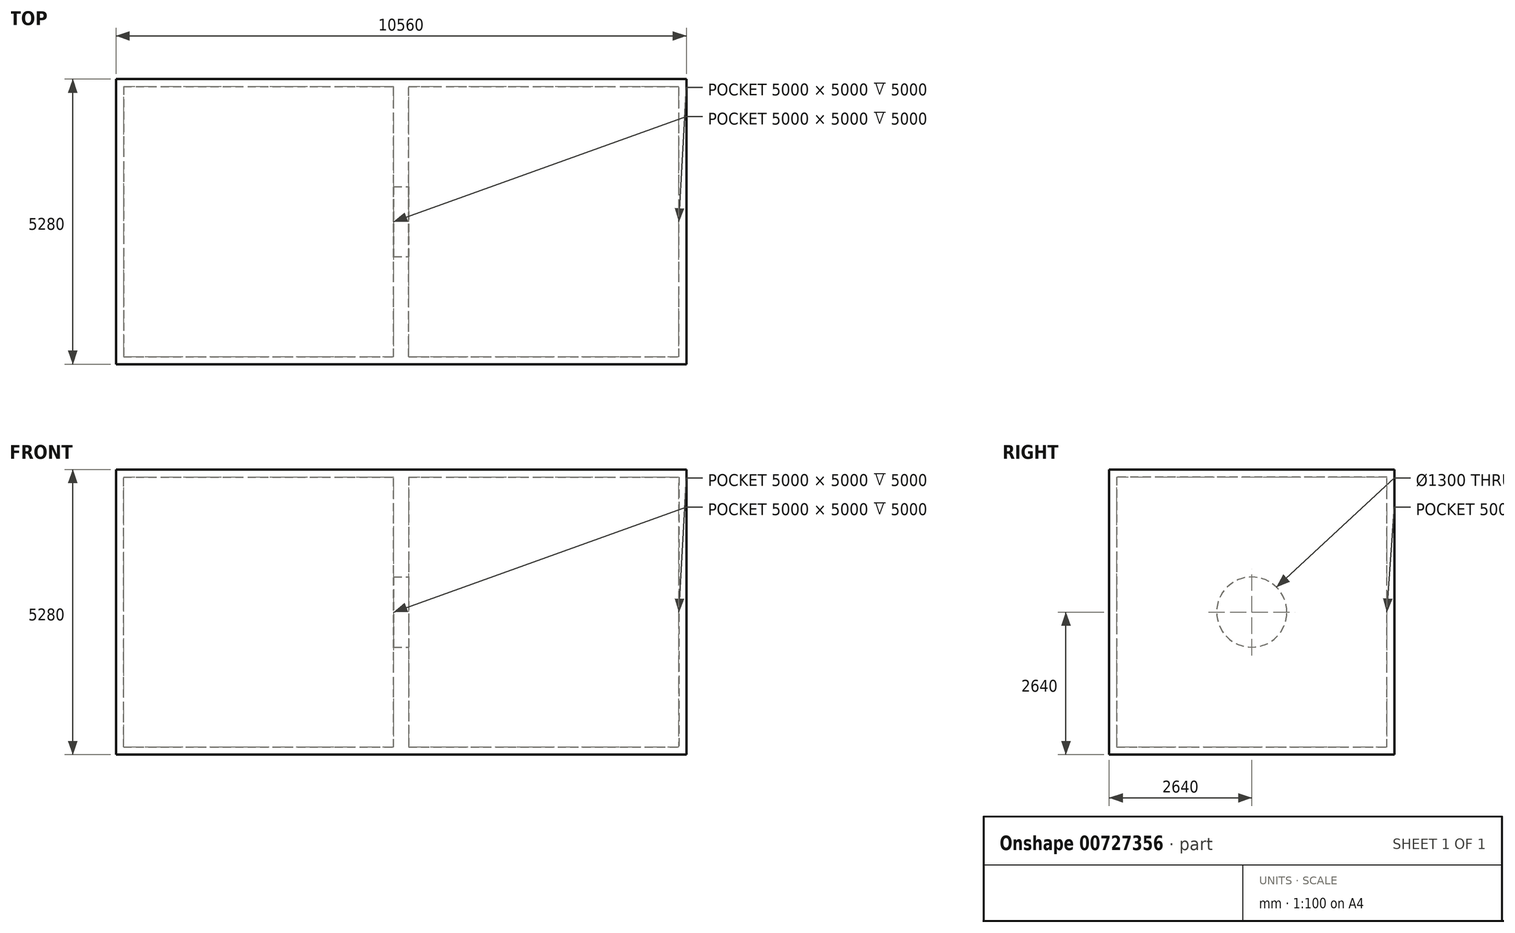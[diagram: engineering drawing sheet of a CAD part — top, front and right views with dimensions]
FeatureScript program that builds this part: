
annotation { "Feature Type Name" : "Feature", "Feature Type Description" : "" }
export const myFeature = defineFeature(function(context is Context, id is Id, definition is map)
    precondition{}
    {
        {
            var Q0;
            Q0=qCreatedBy(makeId("Right.planeOp"),FACE);
            cPlane(context, id + "F0", {"entities" : qUnion([Q0]), "cplaneType" : CPlaneType.OFFSET, "offset" : 5280 * mm, "width" : 150 * mm, "height" : 150 * mm});
        }
        {
            var Q0;
            Q0=qCreatedBy(id+"F0.planeOp",FACE);
            var sketch = newSketch(context, id + "F1", { "sketchPlane" : qUnion([Q0])});
            skLineSegment(sketch, "E0.bottom", {"start": v(-2640, 2640) * mm, "end": v(2640, 2640) * mm});
            skLineSegment(sketch, "E0.top", {"start": v(-2640, -2640) * mm, "end": v(2640, -2640) * mm});
            skLineSegment(sketch, "E0.left", {"start": v(-2640, 2640) * mm, "end": v(-2640, -2640) * mm});
            skLineSegment(sketch, "E0.right", {"start": v(2640, 2640) * mm, "end": v(2640, -2640) * mm});
            skPoint(sketch, "E0.middle", {"position": v(0, 0) * mm});
            skSolve(sketch);
        }
        {
            var Q0;
            Q0=makeQuery(id+"F1.imprint","IMPRINT",FACE,{"disambiguationData":[TD([[makeQuery(id+"F1.imprint","IMPRINT",EDGE,{"derivedFrom":sQuery(id+"F1.wireOp",EDGE,"E0.bottom")}),-1.0]])]});
            extrude(context, id + "F2", {"entities" : qUnion([Q0]), "oppositeDirection" : true, "depth" : 140 * mm, "offsetDistance" : 25 * mm});
        }
        {
            var Q0;
            Q0=makeQuery(id+"F2.opExtrude","CAP_FACE",FACE,{"disambiguationData":[OSD([sQuery(id+"F1.wireOp",EDGE,"E0.bottom"),sQuery(id+"F1.wireOp",EDGE,"E0.top"),sQuery(id+"F1.wireOp",EDGE,"E0.left"),sQuery(id+"F1.wireOp",EDGE,"E0.right")])],"isStart":false});
            var sketch = newSketch(context, id + "F3", { "sketchPlane" : qUnion([Q0])});
            skPoint(sketch, "E1", {"position": v(-2640, 2640) * mm});
            skPoint(sketch, "E2", {"position": v(2640, 2640) * mm});
            skPoint(sketch, "E3", {"position": v(2640, -2640) * mm});
            skPoint(sketch, "E4", {"position": v(-2640, -2640) * mm});
            skPoint(sketch, "E5", {"position": v(-2500, 2640) * mm});
            skPoint(sketch, "E6", {"position": v(-2640, 2500) * mm});
            skPoint(sketch, "E7", {"position": v(2500, 2640) * mm});
            skPoint(sketch, "E8", {"position": v(2640, 2500) * mm});
            skPoint(sketch, "E9", {"position": v(2640, -2500) * mm});
            skPoint(sketch, "E10", {"position": v(2500, -2640) * mm});
            skPoint(sketch, "E11", {"position": v(-2500, -2640) * mm});
            skPoint(sketch, "E12", {"position": v(-2640, -2500) * mm});
            skPoint(sketch, "E13", {"position": v(-2500, 2500) * mm});
            skPoint(sketch, "E14", {"position": v(2500, 2500) * mm});
            skPoint(sketch, "E15", {"position": v(2500, -2500) * mm});
            skPoint(sketch, "E16", {"position": v(-2500, -2500) * mm});
            skLineSegment(sketch, "E17", {"start": v(-2640, 2640) * mm, "end": v(-2640, -2640) * mm});
            skLineSegment(sketch, "E18", {"start": v(-2640, -2640) * mm, "end": v(2640, -2640) * mm});
            skLineSegment(sketch, "E19", {"start": v(2640, -2640) * mm, "end": v(2640, 2640) * mm});
            skLineSegment(sketch, "E20", {"start": v(2640, 2640) * mm, "end": v(-2640, 2640) * mm});
            skLineSegment(sketch, "E21", {"start": v(-2500, 2500) * mm, "end": v(-2500, -2500) * mm});
            skLineSegment(sketch, "E22", {"start": v(-2500, -2500) * mm, "end": v(2500, -2500) * mm});
            skLineSegment(sketch, "E23", {"start": v(2500, -2500) * mm, "end": v(2500, 2500) * mm});
            skLineSegment(sketch, "E24", {"start": v(2500, 2500) * mm, "end": v(-2500, 2500) * mm});
            skSolve(sketch);
        }
        {
            var Q0;
            Q0=makeQuery(id+"F3.imprint","IMPRINT",FACE,{"disambiguationData":[TD([[makeQuery(id+"F3.imprint","IMPRINT",EDGE,{"derivedFrom":sQuery(id+"F3.wireOp",EDGE,"E17")}),1.0]])]});
            extrude(context, id + "F4", {"entities" : qUnion([Q0]), "operationType" : NewBodyOperationType.ADD, "depth" : 5000 * mm, "offsetDistance" : 25 * mm});
        }
        {
            var Q0;
            Q0=makeQuery(id+"F4.opExtrude","CAP_FACE",FACE,{"disambiguationData":[OSD([sQuery(id+"F3.wireOp",EDGE,"E17"),sQuery(id+"F3.wireOp",EDGE,"E18"),sQuery(id+"F3.wireOp",EDGE,"E19"),sQuery(id+"F3.wireOp",EDGE,"E20"),sQuery(id+"F3.wireOp",EDGE,"E21"),sQuery(id+"F3.wireOp",EDGE,"E22"),sQuery(id+"F3.wireOp",EDGE,"E23"),sQuery(id+"F3.wireOp",EDGE,"E24")])],"isStart":false});
            var sketch = newSketch(context, id + "F5", { "sketchPlane" : qUnion([Q0])});
            skPoint(sketch, "E25", {"position": v(-2640, 2640) * mm});
            skPoint(sketch, "E26", {"position": v(2640, 2640) * mm});
            skPoint(sketch, "E27", {"position": v(2640, -2640) * mm});
            skPoint(sketch, "E28", {"position": v(-2640, -2640) * mm});
            skCircle(sketch, "E29", {"center": v(0, 0) * mm, "radius": 650 * mm});
            skSolve(sketch);
        }
        {
            var Q0;
            Q0=makeQuery(id+"F5.imprint","IMPRINT",FACE,{"disambiguationData":[TD([[makeQuery(id+"F5.imprint","IMPRINT",EDGE,{"derivedFrom":sQuery(id+"F5.wireOp",EDGE,"E29")}),-1.0]])]});
            var Q1;
            Q1=makeQuery(id+"F5.imprint","IMPRINT",FACE,{"disambiguationData":[TD([[makeQuery(id+"F5.imprint","IMPRINT",EDGE,{"derivedFrom":makeQuery(id+"F4.opExtrude","CAP_EDGE",EDGE,{"disambiguationData":[OSD([sQuery(id+"F3.wireOp",EDGE,"E17")])],"isStart":false})}),1.0]])]});
            extrude(context, id + "F6", {"entities" : qUnion([Q0, Q1]), "operationType" : NewBodyOperationType.ADD, "depth" : 280 * mm, "offsetDistance" : 25 * mm});
        }
        {
            var Q0;
            Q0=makeQuery(id+"F6.opExtrude","CAP_FACE",FACE,{"disambiguationData":[OSD([sQuery(id+"F3.wireOp",EDGE,"E17"),sQuery(id+"F3.wireOp",EDGE,"E18"),sQuery(id+"F3.wireOp",EDGE,"E19"),sQuery(id+"F3.wireOp",EDGE,"E20"),sQuery(id+"F5.wireOp",EDGE,"E29")])],"isStart":false});
            var sketch = newSketch(context, id + "F7", { "sketchPlane" : qUnion([Q0])});
            skPoint(sketch, "E30", {"position": v(-2640, 2640) * mm});
            skPoint(sketch, "E31", {"position": v(2640, 2640) * mm});
            skPoint(sketch, "E32", {"position": v(2640, -2640) * mm});
            skPoint(sketch, "E33", {"position": v(-2640, -2640) * mm});
            skPoint(sketch, "E34", {"position": v(-2500, -2640) * mm});
            skPoint(sketch, "E35", {"position": v(2500, -2640) * mm});
            skPoint(sketch, "E36", {"position": v(2640, -2500) * mm});
            skPoint(sketch, "E37", {"position": v(2640, 2500) * mm});
            skPoint(sketch, "E38", {"position": v(2500, 2640) * mm});
            skPoint(sketch, "E39", {"position": v(-2500, 2640) * mm});
            skPoint(sketch, "E40", {"position": v(-2640, 2500) * mm});
            skPoint(sketch, "E41", {"position": v(-2640, -2500) * mm});
            skPoint(sketch, "E42", {"position": v(-2500, 2500) * mm});
            skPoint(sketch, "E43", {"position": v(2500, 2500) * mm});
            skPoint(sketch, "E44", {"position": v(2500, -2500) * mm});
            skPoint(sketch, "E45", {"position": v(-2500, -2500) * mm});
            skLineSegment(sketch, "E46", {"start": v(-2640, 2640) * mm, "end": v(2640, 2640) * mm});
            skLineSegment(sketch, "E47", {"start": v(2640, 2640) * mm, "end": v(2640, -2640) * mm});
            skLineSegment(sketch, "E48", {"start": v(2640, -2640) * mm, "end": v(-2640, -2640) * mm});
            skLineSegment(sketch, "E49", {"start": v(-2640, -2640) * mm, "end": v(-2640, 2640) * mm});
            skLineSegment(sketch, "E50", {"start": v(-2500, 2500) * mm, "end": v(2500, 2500) * mm});
            skLineSegment(sketch, "E51", {"start": v(2500, 2500) * mm, "end": v(2500, -2500) * mm});
            skLineSegment(sketch, "E52", {"start": v(2500, -2500) * mm, "end": v(-2500, -2500) * mm});
            skLineSegment(sketch, "E53", {"start": v(-2500, -2500) * mm, "end": v(-2500, 2500) * mm});
            skSolve(sketch);
        }
        {
            var Q0;
            Q0=makeQuery(id+"F7.imprint","IMPRINT",FACE,{"disambiguationData":[TD([[makeQuery(id+"F7.imprint","IMPRINT",EDGE,{"derivedFrom":sQuery(id+"F7.wireOp",EDGE,"E46")}),1.0]])]});
            extrude(context, id + "F8", {"entities" : qUnion([Q0]), "operationType" : NewBodyOperationType.ADD, "depth" : 5000 * mm, "offsetDistance" : 25 * mm});
        }
        {
            var Q0;
            Q0=makeQuery(id+"F8.opExtrude","CAP_FACE",FACE,{"disambiguationData":[OSD([sQuery(id+"F7.wireOp",EDGE,"E46"),sQuery(id+"F7.wireOp",EDGE,"E47"),sQuery(id+"F7.wireOp",EDGE,"E48"),sQuery(id+"F7.wireOp",EDGE,"E49"),sQuery(id+"F7.wireOp",EDGE,"E50"),sQuery(id+"F7.wireOp",EDGE,"E51"),sQuery(id+"F7.wireOp",EDGE,"E52"),sQuery(id+"F7.wireOp",EDGE,"E53")])],"isStart":false});
            var sketch = newSketch(context, id + "F9", { "sketchPlane" : qUnion([Q0])});
            skPoint(sketch, "E54", {"position": v(-2640, 2640) * mm});
            skPoint(sketch, "E55", {"position": v(2640, 2640) * mm});
            skPoint(sketch, "E56", {"position": v(2640, -2640) * mm});
            skPoint(sketch, "E57", {"position": v(-2640, -2640) * mm});
            skLineSegment(sketch, "E58", {"start": v(-2640, 2640) * mm, "end": v(2640, 2640) * mm});
            skLineSegment(sketch, "E59", {"start": v(2640, 2640) * mm, "end": v(2640, -2640) * mm});
            skLineSegment(sketch, "E60", {"start": v(2640, -2640) * mm, "end": v(-2640, -2640) * mm});
            skLineSegment(sketch, "E61", {"start": v(-2640, -2640) * mm, "end": v(-2640, 2640) * mm});
            skSolve(sketch);
        }
        {
            var Q0;
            Q0=makeQuery(id+"F9.imprint","IMPRINT",FACE,{"disambiguationData":[TD([[makeQuery(id+"F9.imprint","IMPRINT",EDGE,{"derivedFrom":sQuery(id+"F9.wireOp",EDGE,"E58")}),1.0]])]});
            var Q1;
            Q1=makeQuery(id+"F9.imprint","IMPRINT",FACE,{"disambiguationData":[TD([[makeQuery(id+"F9.imprint","IMPRINT",EDGE,{"derivedFrom":makeQuery(id+"F8.opExtrude","CAP_EDGE",EDGE,{"disambiguationData":[OSD([sQuery(id+"F7.wireOp",EDGE,"E50")])],"isStart":false})}),-1.0]])]});
            extrude(context, id + "F10", {"entities" : qUnion([Q0, Q1]), "operationType" : NewBodyOperationType.ADD, "depth" : 140 * mm, "offsetDistance" : 25 * mm});
        }
    });
